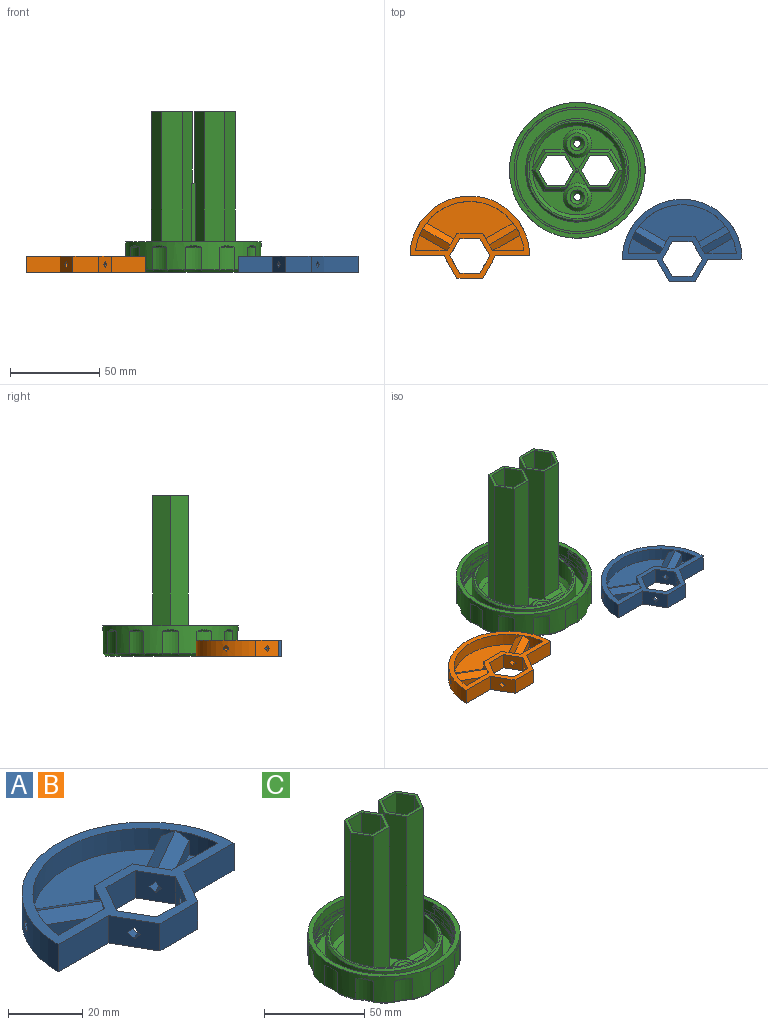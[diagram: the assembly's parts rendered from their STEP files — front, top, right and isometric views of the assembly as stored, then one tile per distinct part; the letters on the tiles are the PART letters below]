
ASSEMBLY  parts=3 mates=2
PART A: 57 faces, bbox 67x46x9 mm
  f0: plane 21.51x13.44mm, normal (-0.35,-0.61,-0.71), area 60.5mm2, adj f1,f3,f13,f32
  f1: plane 21.51x13.44mm, normal (-0.35,-0.61,0.71), area 60.5mm2, adj f0,f2,f13,f32
  f2: plane 21.47x13.46mm, normal (0.35,0.61,0.71), area 60.5mm2, adj f1,f3,f13,f32
  f3: plane 21.47x13.46mm, normal (0.35,0.61,-0.71), area 60.5mm2, adj f0,f2,f13,f32
  f4: plane 21.51x13.44mm, normal (0.35,-0.61,-0.71), area 60.5mm2, adj f5,f7,f19,f32
  f5: plane 21.51x13.44mm, normal (0.35,-0.61,0.71), area 60.5mm2, adj f4,f6,f19,f32
  f6: plane 21.47x13.46mm, normal (-0.35,0.61,0.71), area 60.5mm2, adj f5,f7,f19,f32
  f7: plane 21.47x13.46mm, normal (-0.35,0.61,-0.71), area 60.5mm2, adj f4,f6,f19,f32
  f8: cylinder r=30.5mm len=52.83mm, axis (0,0,-1), area 401.3mm2, adj f11,f34,f40,f41,f42,f48,f49,f50
  f9: plane 3.25x2.17mm, normal (0.87,0.5,0), area 4.1mm2, adj f25,f34,f51
  f10: plane 7x6.25mm, normal (0.87,0.5,0), area 27.7mm2, adj f11,f31,f34,f48,f49,f50
  f11: plane 49.02x21.25mm, normal (0,0,1), area 669.5mm2, adj f8,f10,f22,f31,f41,f48
  f12: plane 9.7x9mm, normal (-0.87,0.5,0), area 94.3mm2, adj f19,f20,f34,f35,f43,f44,f45,f46
  f13: plane 9.7x9mm, normal (0.87,-0.5,0), area 94.3mm2, adj f0,f1,f2,f3,f21,f33,f34,f35
  f14: plane 12.5x9mm, normal (0.87,-0.5,0), area 123.4mm2, adj f29,f30,f34,f35,f43,f44,f45,f46
  f15: plane 0.25x0.17mm, normal (-0.87,0.5,0), area 0mm2, adj f18,f23,f37
  f16: plane 3.25x2.17mm, normal (-0.87,0.5,0), area 4.1mm2, adj f23,f34,f39
  f17: cylinder r=30.5mm len=12.25mm, axis (0,0,-1), area 67.9mm2, adj f18,f23,f34,f37,f38,f39
  f18: plane 17.79x9.15mm, normal (0,0,1), area 85.7mm2, adj f15,f17,f23,f37
  f19: plane 9.7x9mm, normal (-0.87,-0.5,0), area 94.3mm2, adj f4,f5,f6,f7,f12,f33,f34,f35
  f20: plane 11.2x9mm, normal (0,1,0), area 100.8mm2, adj f12,f21,f34,f35
  f21: plane 9.7x9mm, normal (0.87,0.5,0), area 94.3mm2, adj f13,f20,f34,f35,f53,f54,f55,f56
  f22: plane 7x6.25mm, normal (-0.87,0.5,0), area 27.7mm2, adj f11,f31,f34,f40,f41,f42
  f23: plane 17.65x7mm, normal (0,1,0), area 122.2mm2, adj f15,f16,f17,f18,f34,f37,f38,f39
  f24: cylinder r=30.5mm len=12.25mm, axis (0,0,-1), area 67.9mm2, adj f25,f34,f36,f47,f51,f52
  f25: plane 17.65x7mm, normal (0,1,0), area 122.2mm2, adj f9,f24,f26,f34,f36,f47,f51,f52
  f26: plane 0.25x0.17mm, normal (0.87,0.5,0), area 0mm2, adj f25,f36,f47
  f27: plane 19.07x9mm, normal (0,-1,0), area 171.6mm2, adj f28,f32,f34,f35
  f28: plane 12.5x9mm, normal (-0.87,-0.5,0), area 123.4mm2, adj f27,f29,f34,f35,f53,f54,f55,f56
  f29: plane 14.43x9mm, normal (0,-1,0), area 129.9mm2, adj f14,f28,f34,f35
  f30: plane 19.07x9mm, normal (0,-1,0), area 171.6mm2, adj f14,f32,f34,f35
  f31: plane 14.43x7mm, normal (0,1,0), area 101mm2, adj f10,f11,f22,f34
  f32: cylinder r=33.5mm len=67mm, axis (0,0,-1), area 934.2mm2, adj f0,f1,f2,f3,f4,f5,f6,f7
  f33: plane 11.2x9mm, normal (0,-1,0), area 100.8mm2, adj f13,f19,f34,f35
  f34: plane 67x46mm, normal (0,0,1), area 618.2mm2, adj f8,f9,f10,f12,f13,f14,f16,f17
  f35: plane 67x46mm, normal (0,0,-1), area 1707.5mm2, adj f12,f13,f14,f19,f20,f21,f27,f28
  f36: plane 17.79x9.15mm, normal (0,0,1), area 85.7mm2, adj f24,f25,f26,f47
  f37: plane 15.59x9.15mm, normal (-0.25,-0.43,-0.87), area 8.9mm2, adj f15,f17,f18,f23,f38
  f38: plane 15.16x8.75mm, normal (-0.5,-0.87,0), area 78.8mm2, adj f17,f23,f37,f39
  f39: plane 17.33x12.25mm, normal (-0.25,-0.43,0.87), area 80.6mm2, adj f16,f17,f23,f38,f40
  f40: plane 17.54x12.25mm, normal (0.25,0.43,0.87), area 80.6mm2, adj f8,f22,f39,f42
  f41: plane 15.63x9.25mm, normal (0.25,0.43,-0.87), area 8.9mm2, adj f8,f11,f22,f42
  f42: plane 15.37x8.88mm, normal (0.5,0.87,0), area 79.9mm2, adj f8,f22,f40,f41
  f43: plane 3.33x2.96mm, normal (0.35,0.61,0.71), area 7.1mm2, adj f12,f14,f44,f46
  f44: plane 3.33x2.96mm, normal (0.35,0.61,-0.71), area 7.1mm2, adj f12,f14,f43,f45
  f45: plane 3.33x2.96mm, normal (-0.35,-0.61,-0.71), area 7.1mm2, adj f12,f14,f44,f46
  f46: plane 3.33x2.96mm, normal (-0.35,-0.61,0.71), area 7.1mm2, adj f12,f14,f43,f45
  f47: plane 15.59x9.15mm, normal (0.25,-0.43,-0.87), area 8.9mm2, adj f24,f25,f26,f36,f52
  f48: plane 15.63x9.25mm, normal (-0.25,0.43,-0.87), area 8.9mm2, adj f8,f10,f11,f49
  f49: plane 15.37x8.88mm, normal (-0.5,0.87,0), area 79.9mm2, adj f8,f10,f48,f50
  f50: plane 17.54x12.25mm, normal (-0.25,0.43,0.87), area 80.6mm2, adj f8,f10,f49,f51
  f51: plane 17.33x12.25mm, normal (0.25,-0.43,0.87), area 80.6mm2, adj f9,f24,f25,f50,f52
  f52: plane 15.16x8.75mm, normal (0.5,-0.87,0), area 78.8mm2, adj f24,f25,f47,f51
  f53: plane 3.33x2.96mm, normal (0.35,-0.61,0.71), area 7.1mm2, adj f21,f28,f54,f56
  f54: plane 3.33x2.96mm, normal (0.35,-0.61,-0.71), area 7.1mm2, adj f21,f28,f53,f55
  f55: plane 3.33x2.96mm, normal (-0.35,0.61,-0.71), area 7.1mm2, adj f21,f28,f54,f56
  f56: plane 3.33x2.96mm, normal (-0.35,0.61,0.71), area 7.1mm2, adj f21,f28,f53,f55
PART B: same geometry as A
PART C: 112 faces, bbox 77.5x77.5x90.2 mm
  f0: plane 49.91x23.52mm, normal (0,0,1), area 300.2mm2, adj f4,f5,f16,f96,f98,f102,f103,f109
  f1: plane 49.91x23.52mm, normal (0,0,1), area 300.2mm2, adj f16,f74,f81,f97,f99,f100,f101,f108
  f2: plane 72.38x72.38mm, normal (0,0,-1), area 3592.3mm2, adj f45,f46,f47,f48,f49,f50,f51,f52
  f3: plane 12.71x9.14mm, normal (0,0,1), area 40.1mm2, adj f4,f5,f94,f109
  f4: plane 88.19x12.15mm, normal (0.87,-0.5,0), area 958.8mm2, adj f0,f3,f74,f78,f80,f94,f95,f103
  f5: plane 88.19x12.15mm, normal (-0.87,-0.5,0), area 958.8mm2, adj f0,f3,f81,f82,f92,f94,f95,f96
  f6: plane 12.71x9.14mm, normal (0,0,1), area 40.1mm2, adj f74,f81,f93,f108
  f7: cylinder r=38mm len=76mm, axis (0,0,-1), area 2263.6mm2, adj f17,f21,f22,f23,f24,f25,f26,f27
  f8: cylinder r=35.5mm len=71mm, axis (0,0,-1), area 746.4mm2, adj f9,f17,f19
  f9: cylinder r=35.5mm len=71mm, axis (0,0,-1), area 823.7mm2, adj f8,f10
  f10: cylinder r=35.5mm len=71mm, axis (0,0,-1), area 746.4mm2, adj f9,f11,f18
  f11: plane 71x71mm, normal (0,0,1), area 1317.1mm2, adj f10,f13
  f12: cylinder r=27mm len=54mm, axis (0,0,-1), area 1866.1mm2, adj f14,f16
  f13: cylinder r=29mm len=58mm, axis (0,0,-1), area 2186.5mm2, adj f11,f15
  f14: plane 56x56mm, normal (0,0,1), area 172.8mm2, adj f12,f15
  f15: cone r=28mm half-angle=45deg, axis (0,0,-1), area 253.2mm2, adj f13,f14
  f16: cone r=27mm half-angle=45deg, axis (0,0,1), area 460.5mm2, adj f0,f1,f12,f98,f99,f101,f102
  f17: plane 76x76mm, normal (0,0,1), area 577.3mm2, adj f7,f8
  f18: plane 2.31x1.2mm, normal (0,-1,0), area 1.9mm2, adj f10,f20
  f19: plane 2.31x1.2mm, normal (0,1,0), area 1.9mm2, adj f8,f20
  f20: cylinder r=34.3mm len=68.6mm, axis (0,0,1), area 397.1mm2, adj f18,f19
  f21: cylinder r=15mm len=12.5mm, axis (0,0,-1), area 116.8mm2, adj f7,f37,f60
  f22: cylinder r=15mm len=12.5mm, axis (0,0,-1), area 116.8mm2, adj f7,f43,f53
  f23: cylinder r=15mm len=12.5mm, axis (0,0,-1), area 116.8mm2, adj f7,f41,f61
  f24: cylinder r=15mm len=12.5mm, axis (0,0,-1), area 116.8mm2, adj f7,f35,f52
  f25: cylinder r=15mm len=12.5mm, axis (0,0,-1), area 116.8mm2, adj f7,f33,f45
  f26: cylinder r=15mm len=12.5mm, axis (0,0,-1), area 116.8mm2, adj f7,f39,f68
  f27: cylinder r=15mm len=12.5mm, axis (0,0,-1), area 116.8mm2, adj f7,f42,f57
  f28: cylinder r=15mm len=12.5mm, axis (0,0,-1), area 116.8mm2, adj f7,f44,f49
  f29: cylinder r=15mm len=12.5mm, axis (0,0,-1), area 116.8mm2, adj f7,f34,f48
  f30: cylinder r=15mm len=12.5mm, axis (0,0,-1), area 116.8mm2, adj f7,f36,f56
  f31: cylinder r=15mm len=12.5mm, axis (0,0,-1), area 116.8mm2, adj f7,f38,f64
  f32: cylinder r=15mm len=12.5mm, axis (0,0,-1), area 116.8mm2, adj f7,f40,f65
  f33: cone r=15mm half-angle=45deg, axis (0,0,-1), area 6.5mm2, adj f7,f25
  f34: cone r=15mm half-angle=45deg, axis (0,0,-1), area 6.5mm2, adj f7,f29
  f35: cone r=15mm half-angle=45deg, axis (0,0,-1), area 6.5mm2, adj f7,f24
  f36: cone r=15mm half-angle=45deg, axis (0,0,-1), area 6.5mm2, adj f7,f30
  f37: cone r=15mm half-angle=45deg, axis (0,0,-1), area 6.5mm2, adj f7,f21
  f38: cone r=15mm half-angle=45deg, axis (0,0,-1), area 6.5mm2, adj f7,f31
  f39: cone r=15mm half-angle=45deg, axis (0,0,-1), area 6.5mm2, adj f7,f26
  f40: cone r=15mm half-angle=45deg, axis (0,0,-1), area 6.5mm2, adj f7,f32
  f41: cone r=15mm half-angle=45deg, axis (0,0,-1), area 6.5mm2, adj f7,f23
  f42: cone r=15mm half-angle=45deg, axis (0,0,-1), area 6.5mm2, adj f7,f27
  f43: cone r=15mm half-angle=45deg, axis (0,0,-1), area 6.5mm2, adj f7,f22
  f44: cone r=15mm half-angle=45deg, axis (0,0,-1), area 6.5mm2, adj f7,f28
  f45: cone r=16.5mm half-angle=45deg, axis (0,0,-1), area 20.1mm2, adj f2,f25,f46,f47
  f46: cone r=38mm half-angle=45deg, axis (0,0,1), area 21.5mm2, adj f2,f7,f45,f48
  f47: cone r=38mm half-angle=45deg, axis (0,0,1), area 21.5mm2, adj f2,f7,f45,f49
  f48: cone r=16.5mm half-angle=45deg, axis (0,0,-1), area 20.1mm2, adj f2,f29,f46,f50
  f49: cone r=16.5mm half-angle=45deg, axis (0,0,-1), area 20.1mm2, adj f2,f28,f47,f51
  f50: cone r=38mm half-angle=45deg, axis (0,0,1), area 21.5mm2, adj f2,f7,f48,f52
  f51: cone r=38mm half-angle=45deg, axis (0,0,1), area 21.5mm2, adj f2,f7,f49,f53
  f52: cone r=16.5mm half-angle=45deg, axis (0,0,-1), area 20.1mm2, adj f2,f24,f50,f54
  f53: cone r=16.5mm half-angle=45deg, axis (0,0,-1), area 20.1mm2, adj f2,f22,f51,f55
  f54: cone r=38mm half-angle=45deg, axis (0,0,1), area 21.5mm2, adj f2,f7,f52,f56
  f55: cone r=38mm half-angle=45deg, axis (0,0,1), area 21.5mm2, adj f2,f7,f53,f57
  f56: cone r=16.5mm half-angle=45deg, axis (0,0,-1), area 20.1mm2, adj f2,f30,f54,f58
  f57: cone r=16.5mm half-angle=45deg, axis (0,0,-1), area 20.1mm2, adj f2,f27,f55,f59
  f58: cone r=38mm half-angle=45deg, axis (0,0,1), area 21.5mm2, adj f2,f7,f56,f60
  f59: cone r=38mm half-angle=45deg, axis (0,0,1), area 21.5mm2, adj f2,f7,f57,f61
  f60: cone r=16.5mm half-angle=45deg, axis (0,0,-1), area 20.1mm2, adj f2,f21,f58,f62
  f61: cone r=16.5mm half-angle=45deg, axis (0,0,-1), area 20.1mm2, adj f2,f23,f59,f63
  f62: cone r=38mm half-angle=45deg, axis (0,0,1), area 21.5mm2, adj f2,f7,f60,f64
  f63: cone r=38mm half-angle=45deg, axis (0,0,1), area 21.5mm2, adj f2,f7,f61,f65
  f64: cone r=16.5mm half-angle=45deg, axis (0,0,-1), area 20.1mm2, adj f2,f31,f62,f66
  f65: cone r=16.5mm half-angle=45deg, axis (0,0,-1), area 20.1mm2, adj f2,f32,f63,f67
  f66: cone r=38mm half-angle=45deg, axis (0,0,1), area 21.5mm2, adj f2,f7,f64,f68
  f67: cone r=38mm half-angle=45deg, axis (0,0,1), area 21.5mm2, adj f2,f7,f65,f68
  f68: cone r=16.5mm half-angle=45deg, axis (0,0,-1), area 20.1mm2, adj f2,f26,f66,f67
  f69: plane 90x8.43mm, normal (0.87,-0.5,0), area 875.8mm2, adj f2,f70,f79,f80
  f70: plane 90x9.73mm, normal (0,-1,0), area 875.8mm2, adj f2,f69,f71,f80
  f71: plane 90x8.43mm, normal (-0.87,-0.5,0), area 875.8mm2, adj f2,f70,f72,f80
  f72: plane 90x8.43mm, normal (-0.87,0.5,0), area 875.8mm2, adj f2,f71,f73,f80
  f73: plane 90x9.73mm, normal (0,1,0), area 875.8mm2, adj f2,f72,f79,f80
  f74: plane 88.19x12.15mm, normal (0.87,0.5,0), area 958.8mm2, adj f1,f4,f6,f75,f80,f93,f95,f100
  f75: plane 86x11.5mm, normal (0,1,0), area 989mm2, adj f74,f76,f80,f100
  f76: plane 86x9.96mm, normal (-0.87,0.5,0), area 989mm2, adj f75,f77,f80,f101
  f77: plane 86x9.96mm, normal (-0.87,-0.5,0), area 989mm2, adj f76,f78,f80,f102
  f78: plane 86x11.5mm, normal (0,-1,0), area 989mm2, adj f4,f77,f80,f103
  f79: plane 90x8.43mm, normal (0.87,0.5,0), area 875.8mm2, adj f2,f69,f73,f80
  f80: plane 23x19.92mm, normal (0,0,1), area 97.6mm2, adj f4,f69,f70,f71,f72,f73,f74,f75
  f81: plane 88.19x12.15mm, normal (-0.87,0.5,0), area 958.8mm2, adj f1,f5,f6,f91,f92,f93,f95,f97
  f82: plane 86x11.5mm, normal (0,-1,0), area 989mm2, adj f5,f83,f92,f96
  f83: plane 86x9.96mm, normal (0.87,-0.5,0), area 989mm2, adj f82,f84,f92,f98
  f84: plane 86x9.96mm, normal (0.87,0.5,0), area 989mm2, adj f83,f91,f92,f99
  f85: plane 90x8.43mm, normal (-0.87,0.5,0), area 875.8mm2, adj f2,f86,f90,f92
  f86: plane 90x9.73mm, normal (0,1,0), area 875.8mm2, adj f2,f85,f87,f92
  f87: plane 90x8.43mm, normal (0.87,0.5,0), area 875.8mm2, adj f2,f86,f88,f92
  f88: plane 90x8.43mm, normal (0.87,-0.5,0), area 875.8mm2, adj f2,f87,f89,f92
  f89: plane 90x9.73mm, normal (0,-1,0), area 875.8mm2, adj f2,f88,f90,f92
  f90: plane 90x8.43mm, normal (-0.87,-0.5,0), area 875.8mm2, adj f2,f85,f89,f92
  f91: plane 86x11.5mm, normal (0,1,0), area 989mm2, adj f81,f84,f92,f97
  f92: plane 23x19.92mm, normal (0,0,1), area 97.6mm2, adj f5,f81,f82,f83,f84,f85,f86,f87
  f93: plane 48x2.15mm, normal (0,1,0), area 103.4mm2, adj f6,f74,f81,f95
  f94: plane 48x2.15mm, normal (0,-1,0), area 103.4mm2, adj f3,f4,f5,f95
  f95: plane 2.15x2mm, normal (0,0,1), area 3.2mm2, adj f4,f5,f74,f81,f93,f94
  f96: plane 12.65x2mm, normal (0,-0.71,0.71), area 32.5mm2, adj f0,f5,f82,f98
  f97: plane 12.65x2mm, normal (0,0.71,0.71), area 32.5mm2, adj f1,f81,f91,f99
  f98: plane 11.98x7.64mm, normal (0.61,-0.35,0.71), area 35.3mm2, adj f0,f16,f83,f96,f99
  f99: plane 11.98x7.64mm, normal (0.61,0.35,0.71), area 35.3mm2, adj f1,f16,f84,f97,f98
  f100: plane 12.65x2mm, normal (0,0.71,0.71), area 32.5mm2, adj f1,f74,f75,f101
  f101: plane 11.98x7.64mm, normal (-0.61,0.35,0.71), area 35.3mm2, adj f1,f16,f76,f100,f102
  f102: plane 11.98x7.64mm, normal (-0.61,-0.35,0.71), area 35.3mm2, adj f0,f16,f77,f101,f103
  f103: plane 12.65x2mm, normal (0,-0.71,0.71), area 32.5mm2, adj f0,f4,f78,f102
  f104: cylinder r=2mm len=4mm, axis (0,0,-1), area 25.1mm2, adj f2,f110
  f105: cylinder r=2mm len=4mm, axis (0,0,-1), area 25.1mm2, adj f2,f111
  f106: plane 12x12mm, normal (0,0,1), area 62.8mm2, adj f108,f110
  f107: plane 12x12mm, normal (0,0,1), area 62.8mm2, adj f109,f111
  f108: cone r=8mm half-angle=45deg, axis (0,0,-1), area 124.4mm2, adj f1,f6,f74,f81,f106
  f109: cone r=8mm half-angle=45deg, axis (0,0,-1), area 124.4mm2, adj f0,f3,f4,f5,f107
  f110: cone r=2mm half-angle=45deg, axis (0,0,1), area 53.3mm2, adj f104,f106
  f111: cone r=2mm half-angle=45deg, axis (0,0,1), area 53.3mm2, adj f105,f107
PLACE A t=(58.76,-49.77,0)mm
PLACE B t=(-60.22,-47.94,0)mm
PLACE C at identity
MATE planar A.f35 <-> C.f12  axis (0,0,-1) through (58.76,-35.97,0)mm
MATE planar B.f35 <-> C.f2  axis (0,0,-1) through (-60.22,-34.14,0)mm
